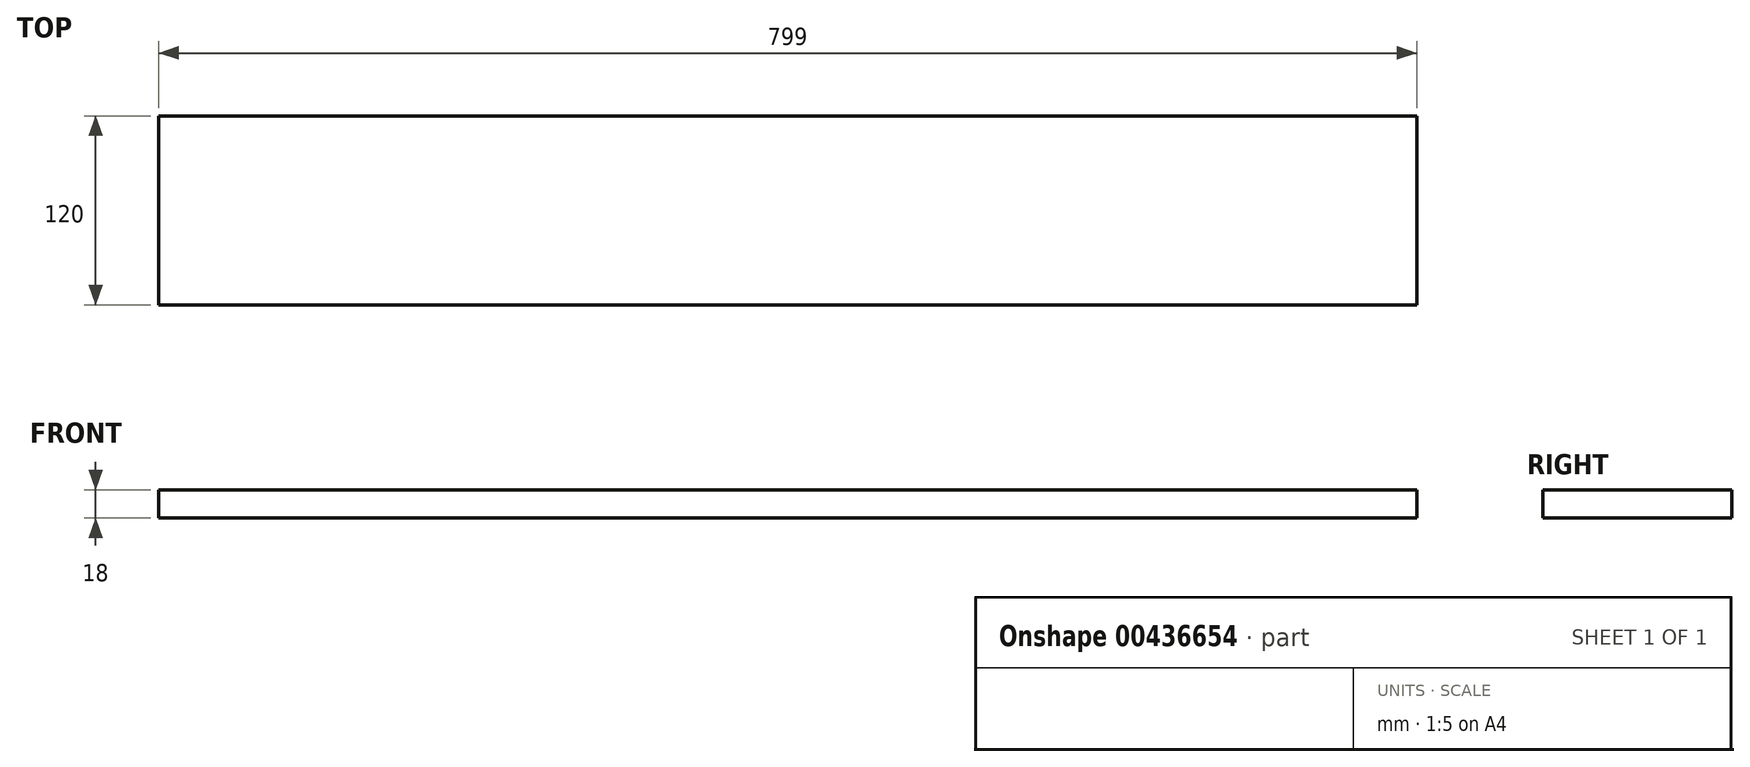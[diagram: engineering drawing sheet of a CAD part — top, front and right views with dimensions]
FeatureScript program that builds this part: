
annotation { "Feature Type Name" : "Feature", "Feature Type Description" : "" }
export const myFeature = defineFeature(function(context is Context, id is Id, definition is map)
    precondition{}
    {
        {
            var Q0;
            Q0=qCreatedBy(makeId("Right.planeOp"),FACE);
            var sketch = newSketch(context, id + "F0", { "sketchPlane" : qUnion([Q0])});
            skLineSegment(sketch, "E0.bottom", {"start": v(60, 9) * mm, "end": v(-60, 9) * mm});
            skLineSegment(sketch, "E0.top", {"start": v(60, -9) * mm, "end": v(-60, -9) * mm});
            skLineSegment(sketch, "E0.left", {"start": v(60, 9) * mm, "end": v(60, -9) * mm});
            skLineSegment(sketch, "E0.right", {"start": v(-60, 9) * mm, "end": v(-60, -9) * mm});
            skPoint(sketch, "E0.middle", {"position": v(0, 0) * mm});
            skSolve(sketch);
        }
        {
            var Q0;
            Q0 = qSketchRegion(id + "F0", true);
            extrude(context, id + "F1", {"entities" : qUnion([Q0]), "depth" : 799 * mm});
        }
    });
